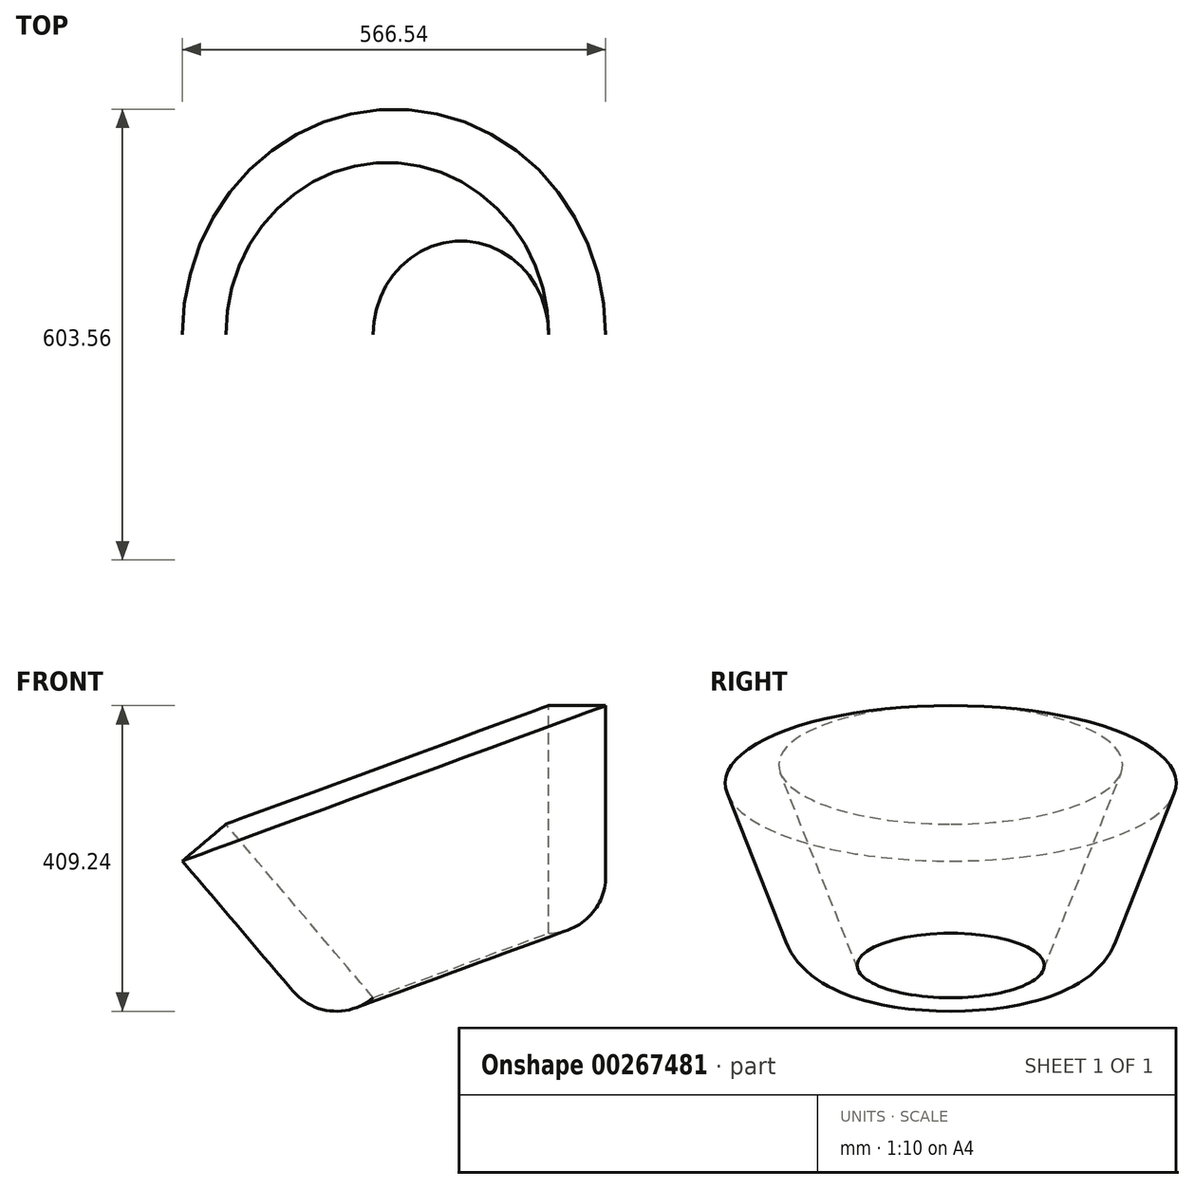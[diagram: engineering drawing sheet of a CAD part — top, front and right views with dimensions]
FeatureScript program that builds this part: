
annotation { "Feature Type Name" : "Feature", "Feature Type Description" : "" }
export const myFeature = defineFeature(function(context is Context, id is Id, definition is map)
    precondition{}
    {
        {
            var Q0;
            Q0=qCreatedBy(makeId("Front.planeOp"),FACE);
            var sketch = newSketch(context, id + "F0", { "sketchPlane" : qUnion([Q0])});
            skLineSegment(sketch, "E0.bottom", {"start": v(2.08, 87.25) * mm, "end": v(78.28, 87.25) * mm});
            skLineSegment(sketch, "E0.top", {"start": v(2.08, -217.55) * mm, "end": v(2.08, -217.55) * mm});
            skLineSegment(sketch, "E0.left", {"start": v(2.08, 87.25) * mm, "end": v(2.08, -217.55) * mm});
            skLineSegment(sketch, "E0.right", {"start": v(78.28, 87.25) * mm, "end": v(78.28, -141.35) * mm});
            skPoint(sketch, "E1.visualSharp", {"position": v(78.28, -217.55) * mm});
            skArc(sketch, "E1.filletArc", {"start": v(2.08, -217.55) * mm, "mid": v(55.97, -195.23) * mm, "end": v(78.28, -141.35) * mm});
            skLineSegment(sketch, "E2", {"start": v(-129.08, -223.44) * mm, "end": v(-247.18, 98.02) * mm});
            skSolve(sketch);
        }
        {
            var Q0;
            Q0=makeQuery(id+"F0.imprint","IMPRINT",FACE,{"disambiguationData":[TD([[makeQuery(id+"F0.imprint","IMPRINT",EDGE,{"derivedFrom":sQuery(id+"F0.wireOp",EDGE,"E0.bottom")}),-1.0]])]});
            var Q1;
            Q1=sQuery(id+"F0.wireOp",EDGE,"E2");
            revolve(context, id + "F1", {"entities" : qUnion([Q0]), "axis" : qUnion([Q1]), "revolveType" : RevolveType.FULL});
        }
    });
